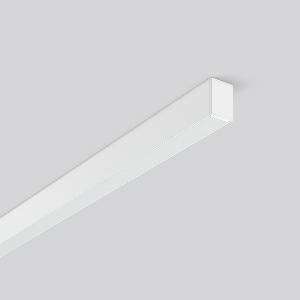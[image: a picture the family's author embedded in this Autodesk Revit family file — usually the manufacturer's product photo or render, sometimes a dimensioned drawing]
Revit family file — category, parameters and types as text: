
# Revit family: less_is_more_27_312196_002_1_76_7788
name_source: partatom
category: Lighting Fixtures
units: mm (PartAtom-declared; Revit-internal decimal feet)

## family parameters
Cut with Voids When Loaded = No
Host = Face
Light Source = No
Part Type = Normal
Room Calculation Point = No
Round Connector Dimension = Use Diameter
Shared = No

## types (1)
- LESS IS MORE 27 (1 x LED Modul 840, 1950 lm, 4000)
    Apparent Load = 25 VA
    CIE Flux Codes = 48 79 96 100 100
    Color Rendering = 80
    Color Temperature = 4000
    Default Elevation = 1800 mm
    Description = Series: LESS IS MORE 27
Ceiling and wall luminaire with slim design. Housing: extruded aluminium profile, powder-coated. End cap aluminium powder-coated. Diffuser made of non-yellowing plastic (PMMA), opal. Suitable for Ceiling mounting, Wall (surface). External driver with connecting cable. 
Colour: traffic white, matt (RAL 9016)
Length: 1012 mm
Width: 28 mm
Height: 38 mm
Lamp: LED
Socket: without socket
Colour temperature: 4000K
Colour rendering index (CRI): 82
System power: 25 W
Rated luminous flux: 1950 lm
Luminous efficiency: 78 lm/W
Control gear: Voltage converter, DALI dim.
Protection class: II
Type of protection: IP 20
    Height = 38 mm
    Lamp = 1 x LED Modul 840
    Lamp Light Flux = 1950 lm
    Lamp count = 1
    Length = 1012 mm
    Lifetime = 50000 h
    Luminous efficacy = 78 lm/W
    Manufacturer = RZB
    ModVariant = No
    Model = 312196.002.1.76
    Mounting Place = Ceiling, Wall
    Mounting Type = Surface mounted
    Number of Poles = 1
    OnlyDefault = Yes
    Power Factor = 1
    Product Name = LESS IS MORE 27
    Product group = Surface mounted LED linear luminaires
    ProductGroupID = 307
    Protection Class = Protection class II
    Protection Degree = IP 20
    RLX_Detail_Level = 1
    RLX_Emergency_Light_Flux = 0 lm
    RLX_Emergency_Type = 0
    RLX_Emergency_Type_DB = No
    RlxData = <blob elided: 22757 chars, md5=30075d95>
    Socket = socket
    Standby Power = 0 W
    System Light Flux = 1950 lm
    System Power = 25 W
    Type Comments = Product without accessories
    Type Image = 312196.002.jpg
    URL = http://relux.com
    VarID = ---
    Voltage = 230 V
    Voltage Range = 220-240 V
    Weight = 0.00 kg
    Width = 28 mm

## geometry (parser evidence)
native form markers: Blend x4, Sweep x13
no freeform markers — native parametric forms only
